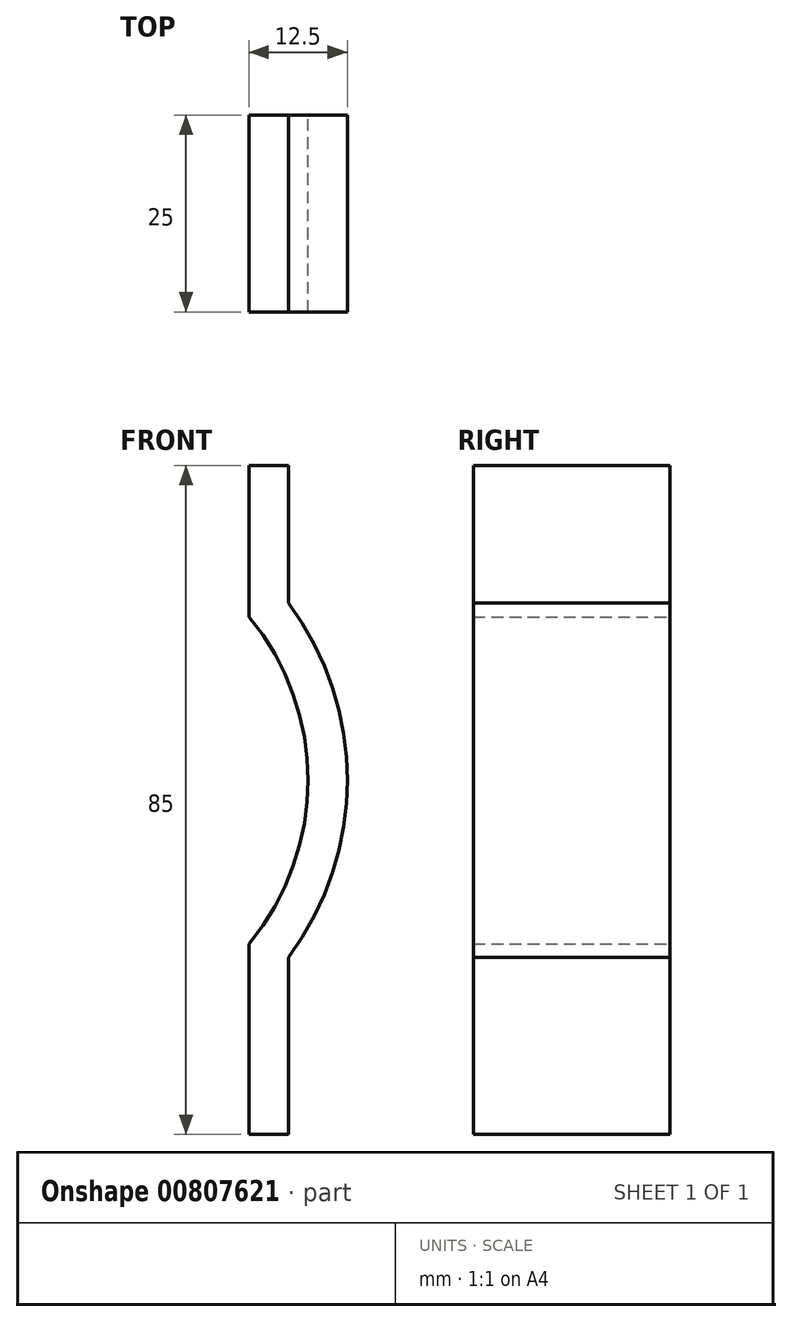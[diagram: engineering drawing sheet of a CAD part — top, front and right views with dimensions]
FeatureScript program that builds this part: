
annotation { "Feature Type Name" : "Feature", "Feature Type Description" : "" }
export const myFeature = defineFeature(function(context is Context, id is Id, definition is map)
    precondition{}
    {
        {
            var Q0;
            Q0=qCreatedBy(makeId("Front.planeOp"),FACE);
            var sketch = newSketch(context, id + "F0", { "sketchPlane" : qUnion([Q0])});
            skLineSegment(sketch, "E0", {"start": v(0, 0) * mm, "end": v(0, -19.23) * mm});
            skPoint(sketch, "E1", {"position": v(-25, -40) * mm});
            skArc(sketch, "E2", {"start": v(0, -60.77) * mm, "mid": v(7.5, -40) * mm, "end": v(0, -19.23) * mm});
            skLineSegment(sketch, "E3.trimOffspring", {"start": v(0, -60.77) * mm, "end": v(0, -85) * mm});
            skLineSegment(sketch, "E4.0", {"start": v(5, -62.5) * mm, "end": v(5, -85) * mm});
            skArc(sketch, "E4.1", {"start": v(5, -62.5) * mm, "mid": v(12.5, -40) * mm, "end": v(5, -17.5) * mm});
            skLineSegment(sketch, "E4.2", {"start": v(5, 0) * mm, "end": v(5, -17.5) * mm});
            skLineSegment(sketch, "E5", {"start": v(0, -85) * mm, "end": v(5, -85) * mm});
            skLineSegment(sketch, "E6", {"start": v(0, 0) * mm, "end": v(5, 0) * mm});
            skSolve(sketch);
        }
        {
            var Q0;
            Q0 = qSketchRegion(id + "F0", true);
            extrude(context, id + "F1", {"entities" : qUnion([Q0]), "depth" : 25 * mm, "offsetDistance" : 25 * mm});
        }
    });
